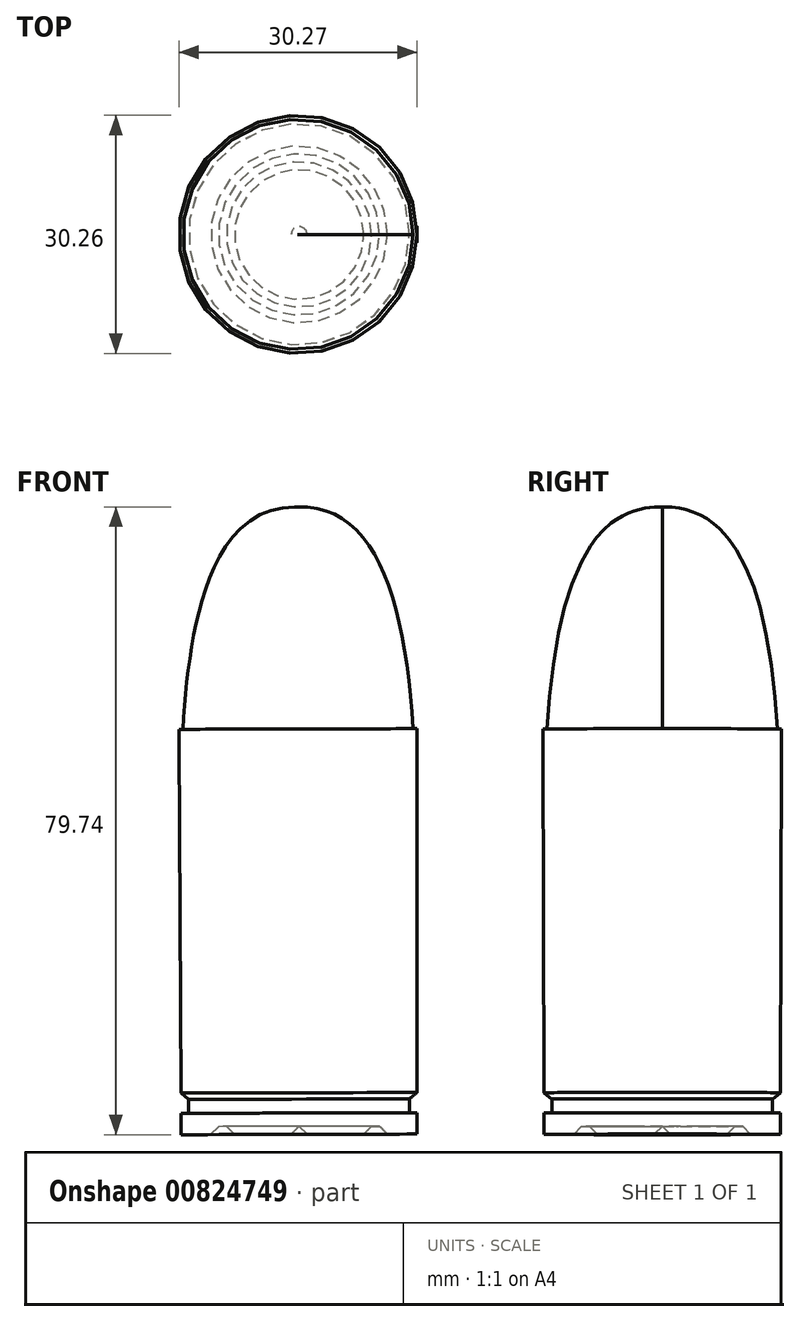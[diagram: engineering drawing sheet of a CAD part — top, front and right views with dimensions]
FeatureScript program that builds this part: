
annotation { "Feature Type Name" : "Feature", "Feature Type Description" : "" }
export const myFeature = defineFeature(function(context is Context, id is Id, definition is map)
    precondition{}
    {
        {
            var Q0;
            Q0=qCreatedBy(makeId("Front.planeOp"),FACE);
            var sketch = newSketch(context, id + "F0", { "sketchPlane" : qUnion([Q0])});
            skLineSegment(sketch, "E0.top", {"start": v(0, 33.27) * mm, "end": v(0.2, 33.27) * mm});
            skLineSegment(sketch, "E0.right", {"start": v(15.2, -46.38) * mm, "end": v(15.2, -43.67) * mm});
            skPoint(sketch, "E0.middle", {"position": v(0, 0) * mm});
            skLineSegment(sketch, "E1", {"start": v(0, 33.27) * mm, "end": v(0.2, -45.38) * mm});
            skPoint(sketch, "E2", {"position": v(8.43, -46.38) * mm});
            skPoint(sketch, "E3", {"position": v(13.43, -46.38) * mm});
            skLineSegment(sketch, "E4.trimOffspring", {"start": v(7.43, -46.38) * mm, "end": v(8.43, -46.38) * mm});
            skLineSegment(sketch, "E5", {"start": v(8.43, -46.38) * mm, "end": v(9.43, -45.38) * mm});
            skLineSegment(sketch, "E6.trimOffspring", {"start": v(13.43, -46.38) * mm, "end": v(15.2, -46.38) * mm});
            skLineSegment(sketch, "E7", {"start": v(9.43, -45.38) * mm, "end": v(10.43, -45.38) * mm});
            skLineSegment(sketch, "E8", {"start": v(13.43, -46.38) * mm, "end": v(11.43, -46.38) * mm});
            skLineSegment(sketch, "E9", {"start": v(10.43, -45.38) * mm, "end": v(11.43, -46.38) * mm});
            skLineSegment(sketch, "E10", {"start": v(1.2, -46.38) * mm, "end": v(0.2, -45.38) * mm});
            skLineSegment(sketch, "E11", {"start": v(1.2, -46.38) * mm, "end": v(7.43, -46.38) * mm});
            skLineSegment(sketch, "E12", {"start": v(15.2, 3.62) * mm, "end": v(15.2, 5.12) * mm});
            skLineSegment(sketch, "E13", {"start": v(15.2, 5.12) * mm, "end": v(14.7, 5.12) * mm});
            skFitSpline(sketch, "E14", {"points": [v(14.7, 5.12) * mm, v(0, 33.27) * mm], "startDerivative": vector(-3.16, 48.7) * mm, "endDerivative": vector(-30.2, -1.08) * mm});
            skLineSegment(sketch, "E15", {"start": v(15.2, -41.1) * mm, "end": v(14.23, -41.9) * mm});
            skLineSegment(sketch, "E16", {"start": v(14.23, -41.9) * mm, "end": v(14.23, -43.67) * mm});
            skLineSegment(sketch, "E17", {"start": v(14.23, -43.67) * mm, "end": v(15.2, -43.67) * mm});
            skLineSegment(sketch, "E18.trimOffspring", {"start": v(15.2, -41.1) * mm, "end": v(15.2, 3.62) * mm});
            skSolve(sketch);
        }
        {
            var Q0;
            Q0=makeQuery(id+"F0.imprint","IMPRINT",FACE,{"disambiguationData":[TD([[makeQuery(id+"F0.imprint","IMPRINT",EDGE,{"derivedFrom":sQuery(id+"F0.wireOp",EDGE,"E0.right")}),1.0]])]});
            var Q1;
            Q1=sQuery(id+"F0.wireOp",EDGE,"E1");
            revolve(context, id + "F1", {"surfaceOperationType" : NewSurfaceOperationType.NEW, "entities" : qUnion([Q0]), "axis" : qUnion([Q1]), "revolveType" : RevolveType.FULL});
        }
    });
